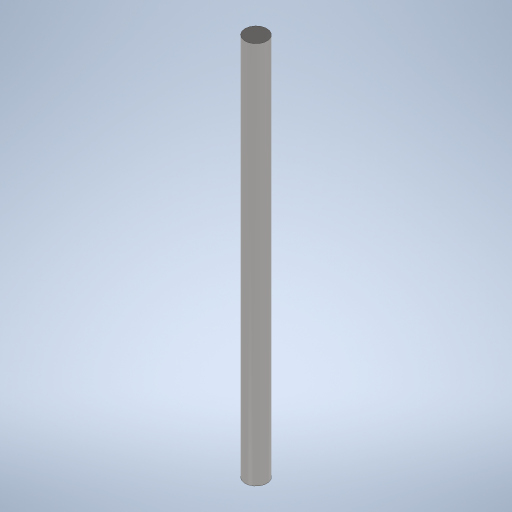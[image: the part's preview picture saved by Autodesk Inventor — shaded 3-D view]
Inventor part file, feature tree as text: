
AUTODESK INVENTOR PART (.ipt)
format: ipt  version: 2023.1 (Build 271208000, 208)  size: 232,960 bytes
history: native  units: mm
features: extrude x1, sketch x1
ambient origin geometry x8: Origin, YZ Plane, XZ Plane, XY Plane, X Axis, Y Axis, Z Axis, Center Point
bodies: Solid1 (feature_tree)
feature tree (2):
  extrude  "Extrusion1"  Depth=70.0mm TaperAngle=0.0deg
  sketch  "Sketch1"  dims[d0=4.0mm d1=70.0mm d2=0.0mm]
